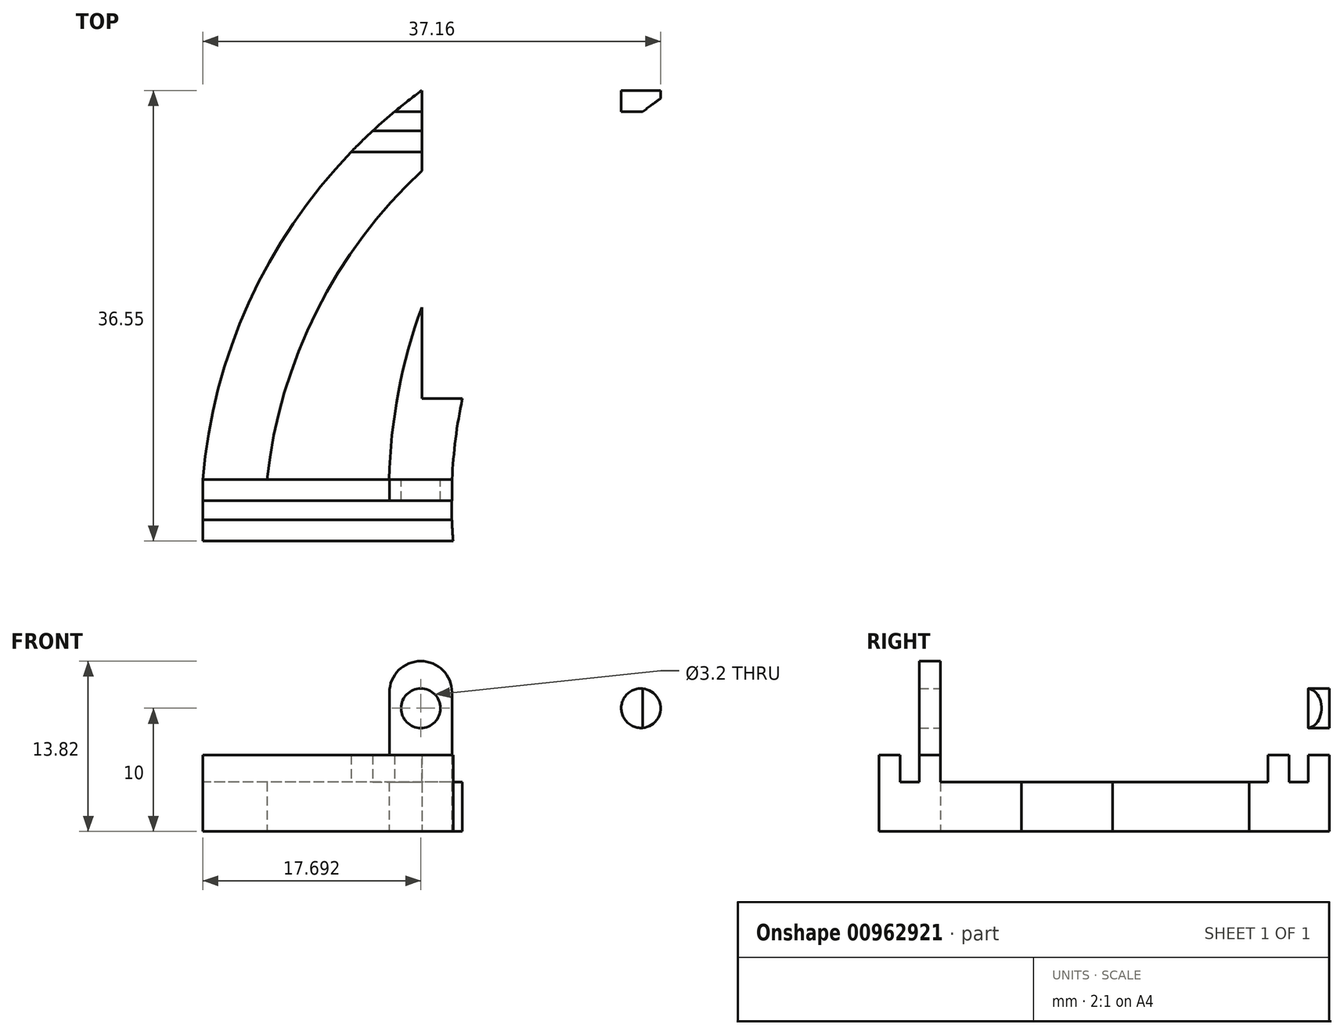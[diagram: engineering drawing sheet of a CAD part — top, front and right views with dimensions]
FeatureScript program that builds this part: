
annotation { "Feature Type Name" : "Feature", "Feature Type Description" : "" }
export const myFeature = defineFeature(function(context is Context, id is Id, definition is map)
    precondition{}
    {
        {
            var Q0;
            Q0=qCreatedBy(makeId("Top.planeOp"),FACE);
            var sketch = newSketch(context, id + "F0", { "sketchPlane" : qUnion([Q0])});
            skLineSegment(sketch, "E0", {"start": v(0, 0) * mm, "end": v(20.32, 0) * mm});
            skLineSegment(sketch, "E1", {"start": v(38.1, 36.55) * mm, "end": v(17.78, 36.55) * mm});
            skLineSegment(sketch, "E2", {"start": v(0, 0) * mm, "end": v(0, 5) * mm});
            skLineSegment(sketch, "E3", {"start": v(17.78, 36.55) * mm, "end": v(17.78, 31.55) * mm});
            skLineSegment(sketch, "E4", {"start": v(38.1, 36.55) * mm, "end": v(38.1, 31.55) * mm});
            skLineSegment(sketch, "E5", {"start": v(20.32, 0) * mm, "end": v(20.32, 5) * mm});
            skPoint(sketch, "E6", {"position": v(20.32, 2.5) * mm});
            skPoint(sketch, "E7", {"position": v(20.32, 3.28) * mm});
            skPoint(sketch, "E8", {"position": v(17.78, 34.05) * mm});
            skPoint(sketch, "E9", {"position": v(17.78, 33.27) * mm});
            skPoint(sketch, "E10.third.point", {"position": v(92.22, -25.68) * mm});
            skCircle(sketch, "E11", {"center": v(43.35, 1.36) * mm, "radius": 43.5 * mm});
            skPoint(sketch, "E11.third.point", {"position": v(84.18, -13.63) * mm});
            skCircle(sketch, "E12", {"center": v(60.2, 3.2) * mm, "radius": 40 * mm});
            skPoint(sketch, "E12.third.point", {"position": v(73.53, -34.5) * mm});
            skLineSegment(sketch, "E13", {"start": v(17.78, 36.55) * mm, "end": v(43.35, 1.36) * mm});
            skLineSegment(sketch, "E14", {"start": v(60.2, 3.2) * mm, "end": v(38.1, 36.55) * mm});
            skPoint(sketch, "E15", {"position": v(20.72, 32.5) * mm});
            skLineSegment(sketch, "E16", {"start": v(38.1, 36.55) * mm, "end": v(35.2, 40.93) * mm});
            skPoint(sketch, "E17", {"position": v(35.34, 40.72) * mm});
            skLineSegment(sketch, "E18", {"start": v(0, 0) * mm, "end": v(43.35, 1.36) * mm});
            skLineSegment(sketch, "E19", {"start": v(20.32, 0) * mm, "end": v(60.2, 3.2) * mm});
            skLineSegment(sketch, "E20", {"start": v(20.32, 0) * mm, "end": v(5.9, -1.16) * mm});
            skPoint(sketch, "E21", {"position": v(15.34, -0.4) * mm});
            skPoint(sketch, "E22", {"position": v(5, 0.16) * mm});
            skCircle(sketch, "E23", {"center": v(45, 0.71) * mm, "radius": 40 * mm});
            skPoint(sketch, "E23.third.point", {"position": v(83.73, 10.68) * mm});
            skCircle(sketch, "E24", {"center": v(58.62, 3.97) * mm, "radius": 43.5 * mm});
            skPoint(sketch, "E24.third.point", {"position": v(88.56, -27.58) * mm});
            skLineSegment(sketch, "E25", {"start": v(-5.82, 0) * mm, "end": v(-5.82, 5) * mm});
            skLineSegment(sketch, "E26", {"start": v(15.13, 5) * mm, "end": v(-5.82, 5) * mm});
            skLineSegment(sketch, "E27", {"start": v(38.1, 31.55) * mm, "end": v(19.52, 31.55) * mm});
            skSolve(sketch);
        }
        {
            var Q0;
            {var subQ2=sQuery(id+"F0.wireOp",EDGE,"E1");Q0=makeQuery(id+"F0.imprint","IMPRINT",FACE,{"disambiguationData":[TD([[makeQuery(id+"F0.imprint","IMPRINT",EDGE,{"derivedFrom":subQ2}),1.0]])]});}
            var Q1;
            {var subQ0=sQuery(id+"F0.wireOp",EDGE,"E24");var subQ1=sQuery(id+"F0.wireOp",EDGE,"E1");var subQ2=makeQuery(id+"F0.imprint","INTERSECT",VERTEX,{"derivedFrom":[subQ1,subQ0]});Q1=makeQuery(id+"F0.imprint","IMPRINT",FACE,{"disambiguationData":[TD([[makeQuery(id+"F0.imprint","IMPRINT",EDGE,{"disambiguationData":[TD([[subQ2,-1.0]])],"derivedFrom":subQ1}),1.0]])]});}
            var Q2;
            {var subQ0=sQuery(id+"F0.wireOp",EDGE,"E23");var subQ1=sQuery(id+"F0.wireOp",EDGE,"E13");var subQ2=makeQuery(id+"F0.imprint","INTERSECT",VERTEX,{"derivedFrom":[subQ1,subQ0]});Q2=makeQuery(id+"F0.imprint","IMPRINT",FACE,{"disambiguationData":[TD([[makeQuery(id+"F0.imprint","IMPRINT",EDGE,{"disambiguationData":[TD([[subQ2,-1.0]])],"derivedFrom":subQ1}),-1.0]])]});}
            var Q3;
            {var subQ0=sQuery(id+"F0.wireOp",EDGE,"E23");var subQ1=makeQuery(id+"F0.imprint","INTERSECT",VERTEX,{"derivedFrom":[subQ0,sQuery(id+"F0.wireOp",EDGE,"E27")]});Q3=makeQuery(id+"F0.imprint","IMPRINT",FACE,{"disambiguationData":[TD([[makeQuery(id+"F0.imprint","IMPRINT",EDGE,{"disambiguationData":[TD([[subQ1,1.0]])],"derivedFrom":subQ0}),-1.0]])]});}
            var Q4;
            {var subQ1=sQuery(id+"F0.wireOp",EDGE,"E1");var subQ3=sQuery(id+"F0.wireOp",EDGE,"E24");var subQ4=makeQuery(id+"F0.imprint","INTERSECT",VERTEX,{"derivedFrom":[subQ1,subQ3]});Q4=makeQuery(id+"F0.imprint","IMPRINT",FACE,{"disambiguationData":[TD([[makeQuery(id+"F0.imprint","IMPRINT",EDGE,{"disambiguationData":[TD([[subQ4,-1.0]])],"derivedFrom":subQ3}),1.0]])]});}
            var Q5;
            {var subQ0=sQuery(id+"F0.wireOp",EDGE,"E27");var subQ1=sQuery(id+"F0.wireOp",EDGE,"E12");var subQ2=makeQuery(id+"F0.imprint","INTERSECT",VERTEX,{"derivedFrom":[subQ1,subQ0]});Q5=makeQuery(id+"F0.imprint","IMPRINT",FACE,{"disambiguationData":[TD([[makeQuery(id+"F0.imprint","IMPRINT",EDGE,{"disambiguationData":[TD([[subQ2,-1.0]])],"derivedFrom":subQ1}),-1.0]])]});}
            var Q6;
            {var subQ1=sQuery(id+"F0.wireOp",EDGE,"E12");var subQ5=sQuery(id+"F0.wireOp",EDGE,"E5");var subQ8=makeQuery(id+"F0.imprint","INTERSECT",VERTEX,{"derivedFrom":[subQ5,subQ1]});Q6=makeQuery(id+"F0.imprint","IMPRINT",FACE,{"disambiguationData":[TD([[makeQuery(id+"F0.imprint","IMPRINT",EDGE,{"disambiguationData":[TD([[subQ8,1.0]])],"derivedFrom":subQ1}),-1.0]])]});}
            var Q7;
            {var subQ0=sQuery(id+"F0.wireOp",EDGE,"E23");var subQ1=sQuery(id+"F0.wireOp",EDGE,"E0");var subQ2=makeQuery(id+"F0.imprint","INTERSECT",VERTEX,{"derivedFrom":[subQ1,subQ0]});Q7=makeQuery(id+"F0.imprint","IMPRINT",FACE,{"disambiguationData":[TD([[makeQuery(id+"F0.imprint","IMPRINT",EDGE,{"disambiguationData":[TD([[subQ2,-1.0]])],"derivedFrom":subQ1}),1.0]])]});}
            var Q8;
            {var subQ1=sQuery(id+"F0.wireOp",EDGE,"E12");var subQ5=sQuery(id+"F0.wireOp",EDGE,"E13");var subQ6=makeQuery(id+"F0.imprint","INTERSECT",VERTEX,{"derivedFrom":[subQ1,subQ5]});Q8=makeQuery(id+"F0.imprint","IMPRINT",FACE,{"disambiguationData":[TD([[makeQuery(id+"F0.imprint","IMPRINT",EDGE,{"disambiguationData":[TD([[subQ6,-1.0]])],"derivedFrom":subQ1}),-1.0]])]});}
            var Q9;
            {var subQ0=sQuery(id+"F0.wireOp",EDGE,"E23");var subQ1=sQuery(id+"F0.wireOp",EDGE,"E18");var subQ2=makeQuery(id+"F0.imprint","INTERSECT",VERTEX,{"derivedFrom":[subQ1,subQ0]});Q9=makeQuery(id+"F0.imprint","IMPRINT",FACE,{"disambiguationData":[TD([[makeQuery(id+"F0.imprint","IMPRINT",EDGE,{"disambiguationData":[TD([[subQ2,-1.0]])],"derivedFrom":subQ1}),1.0]])]});}
            var Q10;
            {var subQ0=sQuery(id+"F0.wireOp",EDGE,"E2");Q10=makeQuery(id+"F0.imprint","IMPRINT",FACE,{"disambiguationData":[TD([[makeQuery(id+"F0.imprint","IMPRINT",EDGE,{"derivedFrom":subQ0}),-1.0]])]});}
            var Q11;
            {var subQ1=sQuery(id+"F0.wireOp",EDGE,"E0");var subQ3=sQuery(id+"F0.wireOp",EDGE,"E23");var subQ4=makeQuery(id+"F0.imprint","INTERSECT",VERTEX,{"derivedFrom":[subQ1,subQ3]});Q11=makeQuery(id+"F0.imprint","IMPRINT",FACE,{"disambiguationData":[TD([[makeQuery(id+"F0.imprint","IMPRINT",EDGE,{"disambiguationData":[TD([[subQ4,1.0]])],"derivedFrom":subQ3}),-1.0]])]});}
            extrude(context, id + "F1", {"entities" : qUnion([Q0, Q1, Q2, Q3, Q4, Q5, Q6, Q7, Q8, Q9, Q10, Q11]), "depth" : 4 * mm, "offsetDistance" : 25 * mm});
        }
        {
            var Q0;
            Q0=makeQuery(id+"F1.opExtrude","CAP_FACE",FACE,{"disambiguationData":[OSD([sQuery(id+"F0.wireOp",EDGE,"E0"),sQuery(id+"F0.wireOp",EDGE,"E1"),sQuery(id+"F0.wireOp",EDGE,"E2"),sQuery(id+"F0.wireOp",EDGE,"E11"),sQuery(id+"F0.wireOp",EDGE,"E12")])],"isStart":true});
            var sketch = newSketch(context, id + "F2", { "sketchPlane" : qUnion([Q0])});
            skLineSegment(sketch, "E28", {"start": v(10.16, 0) * mm, "end": v(10.16, -3) * mm});
            skLineSegment(sketch, "E29.bottom", {"start": v(-2.34, -2.27) * mm, "end": v(22.66, -2.27) * mm});
            skLineSegment(sketch, "E29.top", {"start": v(-2.34, -0.72) * mm, "end": v(22.66, -0.72) * mm});
            skLineSegment(sketch, "E29.left", {"start": v(-2.34, -2.27) * mm, "end": v(-2.34, -0.72) * mm});
            skLineSegment(sketch, "E29.right", {"start": v(22.66, -2.27) * mm, "end": v(22.66, -0.72) * mm});
            skPoint(sketch, "E29.middle", {"position": v(10.16, -1.5) * mm});
            skLineSegment(sketch, "E30", {"start": v(27.94, -36.55) * mm, "end": v(27.94, -33.55) * mm});
            skLineSegment(sketch, "E31.bottom", {"start": v(13.94, -34.28) * mm, "end": v(41.94, -34.28) * mm});
            skLineSegment(sketch, "E31.top", {"start": v(13.94, -35.83) * mm, "end": v(41.94, -35.83) * mm});
            skLineSegment(sketch, "E31.left", {"start": v(13.94, -34.28) * mm, "end": v(13.94, -35.83) * mm});
            skLineSegment(sketch, "E31.right", {"start": v(41.94, -34.28) * mm, "end": v(41.94, -35.83) * mm});
            skPoint(sketch, "E31.middle", {"position": v(27.94, -35.05) * mm});
            skLineSegment(sketch, "E32.bottom", {"start": v(12.94, -36.55) * mm, "end": v(42.94, -36.55) * mm});
            skLineSegment(sketch, "E32.top", {"start": v(12.94, -33.55) * mm, "end": v(42.94, -33.55) * mm});
            skLineSegment(sketch, "E32.left", {"start": v(12.94, -36.55) * mm, "end": v(12.94, -33.55) * mm});
            skLineSegment(sketch, "E32.right", {"start": v(42.94, -36.55) * mm, "end": v(42.94, -33.55) * mm});
            skLineSegment(sketch, "E33.bottom", {"start": v(-4.84, -3) * mm, "end": v(25.16, -3) * mm});
            skLineSegment(sketch, "E33.top", {"start": v(-4.84, 0) * mm, "end": v(25.16, 0) * mm});
            skLineSegment(sketch, "E33.left", {"start": v(-4.84, -3) * mm, "end": v(-4.84, 0) * mm});
            skLineSegment(sketch, "E33.right", {"start": v(25.16, -3) * mm, "end": v(25.16, 0) * mm});
            skPoint(sketch, "E34", {"position": v(20.32, 0) * mm});
            skPoint(sketch, "E35", {"position": v(38.1, -36.55) * mm});
            skPoint(sketch, "E36", {"position": v(17.78, -36.55) * mm});
            skPoint(sketch, "E37", {"position": v(0, 0) * mm});
            skCircle(sketch, "E38", {"center": v(60.2, -3.2) * mm, "radius": 40 * mm});
            skPoint(sketch, "E38.third.point", {"position": v(95.22, -22.51) * mm});
            skCircle(sketch, "E39", {"center": v(39.87, -3.2) * mm, "radius": 40 * mm});
            skPoint(sketch, "E39.third.point", {"position": v(76.99, -18.11) * mm});
            skSolve(sketch);
        }
        {
            var Q0;
            {var subQ0=sQuery(id+"F2.wireOp",EDGE,"E33.top");var subQ1=sQuery(id+"F2.wireOp",EDGE,"E28");var subQ2=makeQuery(id+"F2.imprint","INTERSECT",VERTEX,{"derivedFrom":[subQ1,subQ0]});Q0=makeQuery(id+"F2.imprint","IMPRINT",FACE,{"disambiguationData":[TD([[makeQuery(id+"F2.imprint","IMPRINT",EDGE,{"disambiguationData":[TD([[subQ2,-1.0]])],"derivedFrom":subQ1}),-1.0]])]});}
            var Q1;
            {var subQ0=sQuery(id+"F2.wireOp",EDGE,"E33.top");var subQ1=sQuery(id+"F2.wireOp",EDGE,"E28");var subQ2=makeQuery(id+"F2.imprint","INTERSECT",VERTEX,{"derivedFrom":[subQ1,subQ0]});Q1=makeQuery(id+"F2.imprint","IMPRINT",FACE,{"disambiguationData":[TD([[makeQuery(id+"F2.imprint","IMPRINT",EDGE,{"disambiguationData":[TD([[subQ2,-1.0]])],"derivedFrom":subQ1}),1.0]])]});}
            var Q2;
            {var subQ0=sQuery(id+"F2.wireOp",EDGE,"E33.bottom");var subQ1=sQuery(id+"F2.wireOp",EDGE,"E28");var subQ2=makeQuery(id+"F2.imprint","INTERSECT",VERTEX,{"derivedFrom":[subQ1,subQ0]});Q2=makeQuery(id+"F2.imprint","IMPRINT",FACE,{"disambiguationData":[TD([[makeQuery(id+"F2.imprint","IMPRINT",EDGE,{"disambiguationData":[TD([[subQ2,1.0]])],"derivedFrom":subQ1}),1.0]])]});}
            var Q3;
            {var subQ1=sQuery(id+"F2.wireOp",EDGE,"E33.bottom");var subQ5=sQuery(id+"F2.wireOp",EDGE,"E28");var subQ6=makeQuery(id+"F2.imprint","INTERSECT",VERTEX,{"derivedFrom":[subQ5,subQ1]});Q3=makeQuery(id+"F2.imprint","IMPRINT",FACE,{"disambiguationData":[TD([[makeQuery(id+"F2.imprint","IMPRINT",EDGE,{"disambiguationData":[TD([[subQ6,1.0]])],"derivedFrom":subQ5}),-1.0]])]});}
            var Q4;
            {var subQ0=sQuery(id+"F2.wireOp",EDGE,"E32.top");var subQ1=sQuery(id+"F2.wireOp",EDGE,"E30");var subQ2=makeQuery(id+"F2.imprint","INTERSECT",VERTEX,{"derivedFrom":[subQ1,subQ0]});Q4=makeQuery(id+"F2.imprint","IMPRINT",FACE,{"disambiguationData":[TD([[makeQuery(id+"F2.imprint","IMPRINT",EDGE,{"disambiguationData":[TD([[subQ2,1.0]])],"derivedFrom":subQ1}),-1.0]])]});}
            var Q5;
            {var subQ0=sQuery(id+"F2.wireOp",EDGE,"E32.top");var subQ1=sQuery(id+"F2.wireOp",EDGE,"E30");var subQ2=makeQuery(id+"F2.imprint","INTERSECT",VERTEX,{"derivedFrom":[subQ1,subQ0]});Q5=makeQuery(id+"F2.imprint","IMPRINT",FACE,{"disambiguationData":[TD([[makeQuery(id+"F2.imprint","IMPRINT",EDGE,{"disambiguationData":[TD([[subQ2,1.0]])],"derivedFrom":subQ1}),1.0]])]});}
            var Q6;
            {var subQ0=sQuery(id+"F2.wireOp",EDGE,"E32.bottom");var subQ1=sQuery(id+"F2.wireOp",EDGE,"E30");var subQ2=makeQuery(id+"F2.imprint","INTERSECT",VERTEX,{"derivedFrom":[subQ1,subQ0]});Q6=makeQuery(id+"F2.imprint","IMPRINT",FACE,{"disambiguationData":[TD([[makeQuery(id+"F2.imprint","IMPRINT",EDGE,{"disambiguationData":[TD([[subQ2,-1.0]])],"derivedFrom":subQ1}),-1.0]])]});}
            var Q7;
            {var subQ0=sQuery(id+"F2.wireOp",EDGE,"E32.bottom");var subQ1=sQuery(id+"F2.wireOp",EDGE,"E30");var subQ2=makeQuery(id+"F2.imprint","INTERSECT",VERTEX,{"derivedFrom":[subQ1,subQ0]});Q7=makeQuery(id+"F2.imprint","IMPRINT",FACE,{"disambiguationData":[TD([[makeQuery(id+"F2.imprint","IMPRINT",EDGE,{"disambiguationData":[TD([[subQ2,-1.0]])],"derivedFrom":subQ1}),1.0]])]});}
            extrude(context, id + "F3", {"entities" : qUnion([Q0, Q1, Q2, Q3, Q4, Q5, Q6, Q7]), "operationType" : NewBodyOperationType.ADD, "oppositeDirection" : true, "depth" : 4 * mm, "offsetDistance" : 25 * mm});
        }
        {
            var Q0;
            Q0=makeQuery(id+"F1.opExtrude","CAP_FACE",FACE,{"disambiguationData":[OSD([sQuery(id+"F0.wireOp",EDGE,"E0"),sQuery(id+"F0.wireOp",EDGE,"E1"),sQuery(id+"F0.wireOp",EDGE,"E2"),sQuery(id+"F0.wireOp",EDGE,"E11"),sQuery(id+"F0.wireOp",EDGE,"E12"),sQuery(id+"F0.wireOp",EDGE,"E23"),sQuery(id+"F0.wireOp",EDGE,"E24"),sQuery(id+"F0.wireOp",EDGE,"E26"),sQuery(id+"F0.wireOp",EDGE,"E27")])],"isStart":false});
            var sketch = newSketch(context, id + "F4", { "sketchPlane" : qUnion([Q0])});
            skLineSegment(sketch, "E40", {"start": v(26.43, 36.55) * mm, "end": v(26.43, 31.55) * mm});
            skLineSegment(sketch, "E41.bottom", {"start": v(11.43, 34.83) * mm, "end": v(41.43, 34.83) * mm});
            skLineSegment(sketch, "E41.top", {"start": v(11.43, 33.28) * mm, "end": v(41.43, 33.28) * mm});
            skLineSegment(sketch, "E41.left", {"start": v(11.43, 34.83) * mm, "end": v(11.43, 33.28) * mm});
            skLineSegment(sketch, "E41.right", {"start": v(41.43, 34.83) * mm, "end": v(41.43, 33.28) * mm});
            skPoint(sketch, "E41.middle", {"position": v(26.43, 34.05) * mm});
            skLineSegment(sketch, "E42", {"start": v(10.16, 0) * mm, "end": v(10.16, 5) * mm});
            skLineSegment(sketch, "E43.bottom", {"start": v(27.66, 3.27) * mm, "end": v(-7.34, 3.27) * mm});
            skLineSegment(sketch, "E43.top", {"start": v(27.66, 1.72) * mm, "end": v(-7.34, 1.72) * mm});
            skLineSegment(sketch, "E43.left", {"start": v(27.66, 3.27) * mm, "end": v(27.66, 1.72) * mm});
            skLineSegment(sketch, "E43.right", {"start": v(-7.34, 3.27) * mm, "end": v(-7.34, 1.72) * mm});
            skPoint(sketch, "E43.middle", {"position": v(10.16, 2.5) * mm});
            skLineSegment(sketch, "E44.bottom", {"start": v(30.16, 5) * mm, "end": v(-9.84, 5) * mm});
            skLineSegment(sketch, "E44.top", {"start": v(30.16, 0) * mm, "end": v(-9.84, 0) * mm});
            skLineSegment(sketch, "E44.left", {"start": v(30.16, 5) * mm, "end": v(30.16, 0) * mm});
            skLineSegment(sketch, "E44.right", {"start": v(-9.84, 5) * mm, "end": v(-9.84, 0) * mm});
            skLineSegment(sketch, "E45.bottom", {"start": v(46.43, 36.55) * mm, "end": v(6.43, 36.55) * mm});
            skLineSegment(sketch, "E45.top", {"start": v(46.43, 31.55) * mm, "end": v(6.43, 31.55) * mm});
            skLineSegment(sketch, "E45.left", {"start": v(46.43, 36.55) * mm, "end": v(46.43, 31.55) * mm});
            skLineSegment(sketch, "E45.right", {"start": v(6.43, 36.55) * mm, "end": v(6.43, 31.55) * mm});
            skSolve(sketch);
        }
        {
            var Q0;
            {var subQ0=sQuery(id+"F4.wireOp",EDGE,"E45.bottom");var subQ1=sQuery(id+"F4.wireOp",EDGE,"E40");var subQ2=makeQuery(id+"F4.imprint","INTERSECT",VERTEX,{"derivedFrom":[subQ1,subQ0]});Q0=makeQuery(id+"F4.imprint","IMPRINT",FACE,{"disambiguationData":[TD([[makeQuery(id+"F4.imprint","IMPRINT",EDGE,{"disambiguationData":[TD([[subQ2,-1.0]])],"derivedFrom":subQ1}),-1.0]])]});}
            var Q1;
            {var subQ0=sQuery(id+"F4.wireOp",EDGE,"E45.bottom");var subQ1=sQuery(id+"F4.wireOp",EDGE,"E40");var subQ2=makeQuery(id+"F4.imprint","INTERSECT",VERTEX,{"derivedFrom":[subQ1,subQ0]});Q1=makeQuery(id+"F4.imprint","IMPRINT",FACE,{"disambiguationData":[TD([[makeQuery(id+"F4.imprint","IMPRINT",EDGE,{"disambiguationData":[TD([[subQ2,-1.0]])],"derivedFrom":subQ1}),1.0]])]});}
            var Q2;
            {var subQ0=sQuery(id+"F4.wireOp",EDGE,"E44.top");var subQ1=sQuery(id+"F4.wireOp",EDGE,"E42");var subQ2=makeQuery(id+"F4.imprint","INTERSECT",VERTEX,{"derivedFrom":[subQ1,subQ0]});Q2=makeQuery(id+"F4.imprint","IMPRINT",FACE,{"disambiguationData":[TD([[makeQuery(id+"F4.imprint","IMPRINT",EDGE,{"disambiguationData":[TD([[subQ2,-1.0]])],"derivedFrom":subQ1}),-1.0]])]});}
            var Q3;
            {var subQ0=sQuery(id+"F4.wireOp",EDGE,"E44.top");var subQ1=sQuery(id+"F4.wireOp",EDGE,"E42");var subQ2=makeQuery(id+"F4.imprint","INTERSECT",VERTEX,{"derivedFrom":[subQ1,subQ0]});Q3=makeQuery(id+"F4.imprint","IMPRINT",FACE,{"disambiguationData":[TD([[makeQuery(id+"F4.imprint","IMPRINT",EDGE,{"disambiguationData":[TD([[subQ2,-1.0]])],"derivedFrom":subQ1}),1.0]])]});}
            var Q4;
            {var subQ0=sQuery(id+"F4.wireOp",EDGE,"E45.top");var subQ1=sQuery(id+"F4.wireOp",EDGE,"E40");var subQ2=makeQuery(id+"F4.imprint","INTERSECT",VERTEX,{"derivedFrom":[subQ1,subQ0]});Q4=makeQuery(id+"F4.imprint","IMPRINT",FACE,{"disambiguationData":[TD([[makeQuery(id+"F4.imprint","IMPRINT",EDGE,{"disambiguationData":[TD([[subQ2,1.0]])],"derivedFrom":subQ1}),1.0]])]});}
            var Q5;
            {var subQ0=sQuery(id+"F4.wireOp",EDGE,"E44.bottom");var subQ2=sQuery(id+"F4.wireOp",EDGE,"E42");var subQ3=makeQuery(id+"F4.imprint","INTERSECT",VERTEX,{"derivedFrom":[subQ2,subQ0]});Q5=makeQuery(id+"F4.imprint","IMPRINT",FACE,{"disambiguationData":[TD([[makeQuery(id+"F4.imprint","IMPRINT",EDGE,{"disambiguationData":[TD([[subQ3,1.0]])],"derivedFrom":subQ2}),-1.0]])]});}
            var Q6;
            {var subQ0=sQuery(id+"F4.wireOp",EDGE,"E44.bottom");var subQ2=sQuery(id+"F4.wireOp",EDGE,"E42");var subQ3=makeQuery(id+"F4.imprint","INTERSECT",VERTEX,{"derivedFrom":[subQ2,subQ0]});Q6=makeQuery(id+"F4.imprint","IMPRINT",FACE,{"disambiguationData":[TD([[makeQuery(id+"F4.imprint","IMPRINT",EDGE,{"disambiguationData":[TD([[subQ3,1.0]])],"derivedFrom":subQ2}),1.0]])]});}
            var Q7;
            {var subQ0=sQuery(id+"F4.wireOp",EDGE,"E45.top");var subQ3=sQuery(id+"F4.wireOp",EDGE,"E40");var subQ4=makeQuery(id+"F4.imprint","INTERSECT",VERTEX,{"derivedFrom":[subQ3,subQ0]});Q7=makeQuery(id+"F4.imprint","IMPRINT",FACE,{"disambiguationData":[TD([[makeQuery(id+"F4.imprint","IMPRINT",EDGE,{"disambiguationData":[TD([[subQ4,1.0]])],"derivedFrom":subQ3}),-1.0]])]});}
            extrude(context, id + "F5", {"entities" : qUnion([Q0, Q1, Q2, Q3, Q4, Q5, Q6, Q7]), "operationType" : NewBodyOperationType.ADD, "depth" : 2.2 * mm, "offsetDistance" : 25 * mm});
        }
        {
            var Q0;
            Q0=makeQuery(id+"F5.opExtrude","CAP_FACE",FACE,{"disambiguationData":[OSD([sQuery(id+"F0.wireOp",EDGE,"E11"),sQuery(id+"F0.wireOp",EDGE,"E12"),sQuery(id+"F4.wireOp",EDGE,"E41.bottom"),sQuery(id+"F4.wireOp",EDGE,"E45.bottom")])],"isStart":false});
            var sketch = newSketch(context, id + "F6", { "sketchPlane" : qUnion([Q0])});
            skLineSegment(sketch, "E46.bottom", {"start": v(38.1, 36.55) * mm, "end": v(33.02, 36.55) * mm});
            skLineSegment(sketch, "E46.top", {"start": v(38.1, 34.83) * mm, "end": v(33.02, 34.83) * mm});
            skLineSegment(sketch, "E46.left", {"start": v(38.1, 36.55) * mm, "end": v(38.1, 34.83) * mm});
            skLineSegment(sketch, "E46.right", {"start": v(33.02, 36.55) * mm, "end": v(33.02, 34.83) * mm});
            skSolve(sketch);
        }
        {
            var Q0;
            Q0=makeQuery(id+"F6.imprint","IMPRINT",FACE,{"disambiguationData":[TD([[makeQuery(id+"F6.imprint","IMPRINT",EDGE,{"derivedFrom":sQuery(id+"F6.wireOp",EDGE,"E46.bottom")}),1.0]])]});
            extrude(context, id + "F7", {"entities" : qUnion([Q0]), "operationType" : NewBodyOperationType.ADD, "depth" : 7.62 * mm, "offsetDistance" : 25 * mm});
        }
        {
            var Q0;
            Q0=makeQuery(id+"F5.opExtrude","CAP_FACE",FACE,{"disambiguationData":[OSD([sQuery(id+"F0.wireOp",EDGE,"E2"),sQuery(id+"F0.wireOp",EDGE,"E12"),sQuery(id+"F4.wireOp",EDGE,"E43.bottom"),sQuery(id+"F4.wireOp",EDGE,"E44.bottom")])],"isStart":false});
            var sketch = newSketch(context, id + "F8", { "sketchPlane" : qUnion([Q0])});
            skLineSegment(sketch, "E47.bottom", {"start": v(20.23, 5) * mm, "end": v(15.15, 5) * mm});
            skLineSegment(sketch, "E47.top", {"start": v(20.23, 3.27) * mm, "end": v(15.15, 3.27) * mm});
            skLineSegment(sketch, "E47.left", {"start": v(20.23, 5) * mm, "end": v(20.23, 3.27) * mm});
            skLineSegment(sketch, "E47.right", {"start": v(15.15, 5) * mm, "end": v(15.15, 3.27) * mm});
            skSolve(sketch);
        }
        {
            var Q0;
            Q0 = qSketchRegion(id + "F8", true);
            extrude(context, id + "F9", {"entities" : qUnion([Q0]), "operationType" : NewBodyOperationType.ADD, "depth" : 7.62 * mm, "offsetDistance" : 25 * mm});
        }
        {
            var Q0;
            Q0=makeQuery(id+"F9.opExtrude","CAP_EDGE",EDGE,{"disambiguationData":[OSD([sQuery(id+"F8.wireOp",EDGE,"E47.right")])],"isStart":false});
            var Q1;
            Q1=makeQuery(id+"F9.opExtrude","CAP_EDGE",EDGE,{"disambiguationData":[OSD([sQuery(id+"F8.wireOp",EDGE,"E47.left")])],"isStart":false});
            var Q2;
            Q2=makeQuery(id+"F7.opExtrude","CAP_EDGE",EDGE,{"disambiguationData":[OSD([sQuery(id+"F6.wireOp",EDGE,"E46.right")])],"isStart":false});
            fillet(context, id + "F10", {"entities" : qUnion([Q0, Q1, Q2]), "radius" : 2.54 * mm, "tangentPropagation" : true, "allowEdgeOverflow" : false});
        }
        {
            var Q0;
            Q0=makeQuery(id+"F7.boolean.opBoolean","MERGE",FACE,{"derivedFrom":[makeQuery(id+"F5.boolean.opBoolean","MERGE",FACE,{"derivedFrom":[makeQuery(id+"F1.opExtrude","SWEPT_FACE",FACE,{"disambiguationData":[OSD([sQuery(id+"F0.wireOp",EDGE,"E1")])]}),makeQuery(id+"F5.opExtrude","SWEPT_FACE",FACE,{"disambiguationData":[OSD([sQuery(id+"F4.wireOp",EDGE,"E45.bottom")])]})]}),makeQuery(id+"F7.opExtrude","SWEPT_FACE",FACE,{"disambiguationData":[OSD([sQuery(id+"F6.wireOp",EDGE,"E46.bottom")])]})]});
            var sketch = newSketch(context, id + "F11", { "sketchPlane" : qUnion([Q0])});
            skLineSegment(sketch, "E48", {"start": v(-33.02, 6.2) * mm, "end": v(-33.02, 10) * mm});
            skLineSegment(sketch, "E49", {"start": v(-33.02, 10) * mm, "end": v(-38.1, 10) * mm});
            skCircle(sketch, "E50", {"center": v(-35.56, 10) * mm, "radius": 1.6 * mm});
            skSolve(sketch);
        }
        {
            var Q0;
            Q0=makeQuery(id+"F9.boolean.opBoolean","MERGE",FACE,{"derivedFrom":[makeQuery(id+"F5.boolean.opBoolean","MERGE",FACE,{"derivedFrom":[makeQuery(id+"F1.opExtrude","SWEPT_FACE",FACE,{"disambiguationData":[OSD([sQuery(id+"F0.wireOp",EDGE,"E26")])]}),makeQuery(id+"F5.opExtrude","SWEPT_FACE",FACE,{"disambiguationData":[OSD([sQuery(id+"F4.wireOp",EDGE,"E44.bottom")])]})]}),makeQuery(id+"F9.opExtrude","SWEPT_FACE",FACE,{"disambiguationData":[OSD([sQuery(id+"F8.wireOp",EDGE,"E47.bottom")])]})]});
            var sketch = newSketch(context, id + "F12", { "sketchPlane" : qUnion([Q0])});
            skLineSegment(sketch, "E51", {"start": v(-15.15, 6.2) * mm, "end": v(-15.15, 10) * mm});
            skPoint(sketch, "E51.endSnap0", {"position": v(-15.15, 8.74) * mm});
            skLineSegment(sketch, "E52", {"start": v(-15.15, 10) * mm, "end": v(-20.23, 10) * mm});
            skCircle(sketch, "E53", {"center": v(-17.7, 10) * mm, "radius": 1.6 * mm});
            skSolve(sketch);
        }
        {
            var Q0;
            {var subQ0=sQuery(id+"F12.wireOp",EDGE,"E53");var subQ1=sQuery(id+"F12.wireOp",EDGE,"E52");var subQ2=makeQuery(id+"F12.imprint","INTERSECT",VERTEX,{"disambiguationData":[OD(0.0)],"derivedFrom":[subQ1,subQ0]});Q0=makeQuery(id+"F12.imprint","IMPRINT",FACE,{"disambiguationData":[TD([[makeQuery(id+"F12.imprint","IMPRINT",EDGE,{"disambiguationData":[TD([[subQ2,-1.0]])],"derivedFrom":subQ1}),1.0]])]});}
            var Q1;
            {var subQ0=sQuery(id+"F12.wireOp",EDGE,"E53");var subQ1=sQuery(id+"F12.wireOp",EDGE,"E52");var subQ2=makeQuery(id+"F12.imprint","INTERSECT",VERTEX,{"disambiguationData":[OD(0.0)],"derivedFrom":[subQ1,subQ0]});Q1=makeQuery(id+"F12.imprint","IMPRINT",FACE,{"disambiguationData":[TD([[makeQuery(id+"F12.imprint","IMPRINT",EDGE,{"disambiguationData":[TD([[subQ2,-1.0]])],"derivedFrom":subQ1}),-1.0]])]});}
            var Q2;
            {var subQ0=sQuery(id+"F11.wireOp",EDGE,"E50");var subQ1=sQuery(id+"F11.wireOp",EDGE,"E49");var subQ2=makeQuery(id+"F11.imprint","INTERSECT",VERTEX,{"disambiguationData":[OD(0.0)],"derivedFrom":[subQ1,subQ0]});Q2=makeQuery(id+"F11.imprint","IMPRINT",FACE,{"disambiguationData":[TD([[makeQuery(id+"F11.imprint","IMPRINT",EDGE,{"disambiguationData":[TD([[subQ2,-1.0]])],"derivedFrom":subQ1}),1.0]])]});}
            var Q3;
            {var subQ0=sQuery(id+"F11.wireOp",EDGE,"E50");var subQ1=sQuery(id+"F11.wireOp",EDGE,"E49");var subQ2=makeQuery(id+"F11.imprint","INTERSECT",VERTEX,{"disambiguationData":[OD(0.0)],"derivedFrom":[subQ1,subQ0]});Q3=makeQuery(id+"F11.imprint","IMPRINT",FACE,{"disambiguationData":[TD([[makeQuery(id+"F11.imprint","IMPRINT",EDGE,{"disambiguationData":[TD([[subQ2,-1.0]])],"derivedFrom":subQ1}),-1.0]])]});}
            extrude(context, id + "F13", {"entities" : qUnion([Q0, Q1, Q2, Q3]), "operationType" : NewBodyOperationType.REMOVE, "oppositeDirection" : true, "depth" : 25 * mm, "offsetDistance" : 25 * mm});
        }
    });
